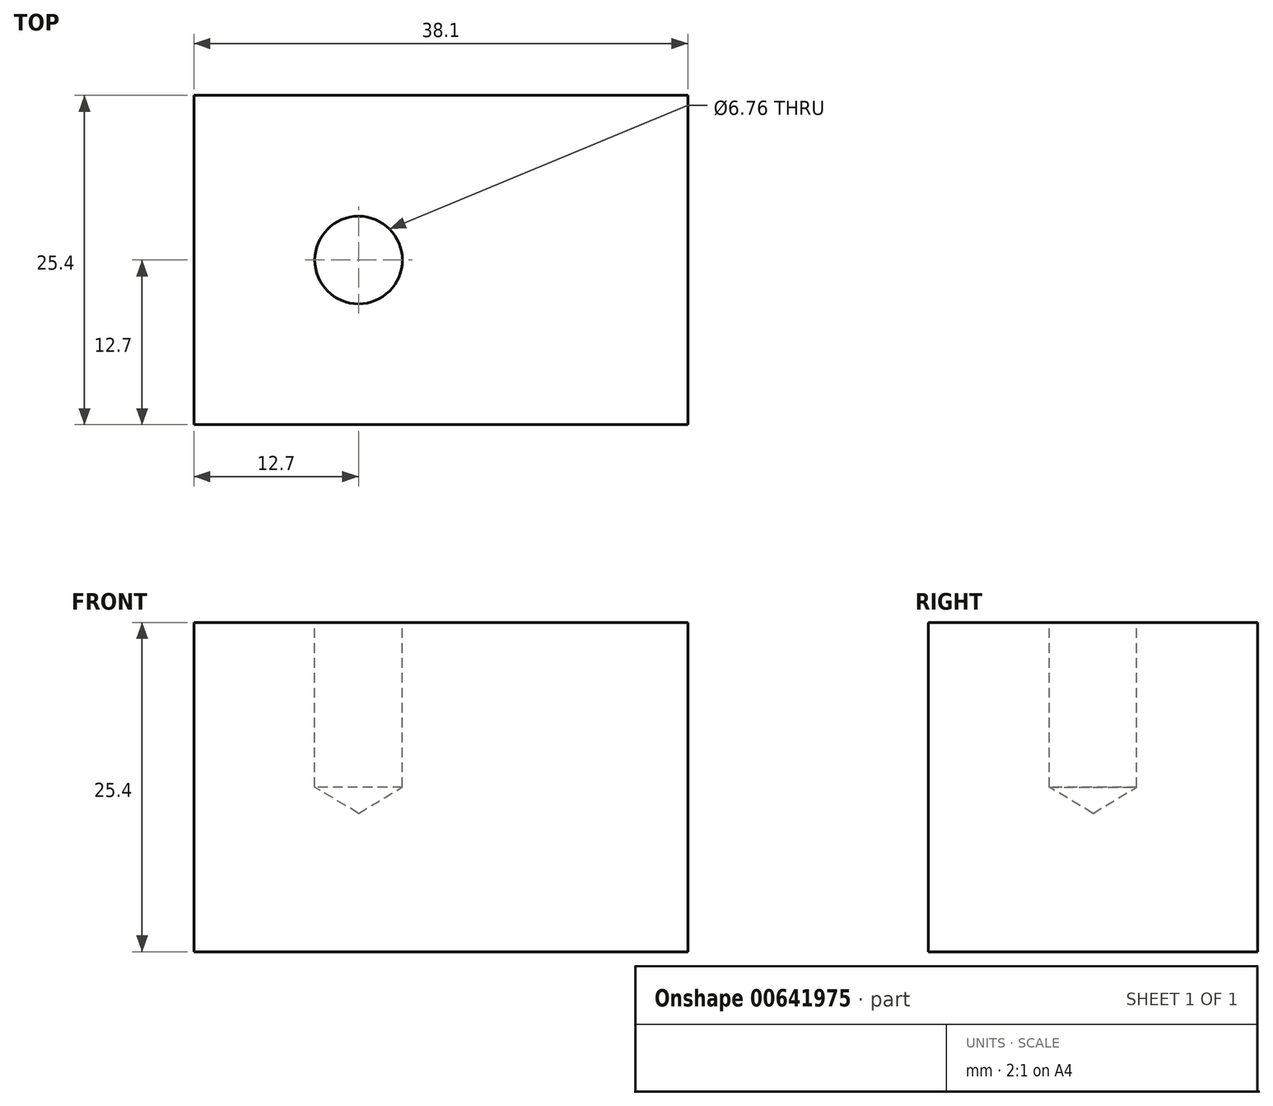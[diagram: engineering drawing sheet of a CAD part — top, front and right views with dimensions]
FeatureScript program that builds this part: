
annotation { "Feature Type Name" : "Feature", "Feature Type Description" : "" }
export const myFeature = defineFeature(function(context is Context, id is Id, definition is map)
    precondition{}
    {
        {
            var Q0;
            Q0=qCreatedBy(makeId("Top.planeOp"),FACE);
            var sketch = newSketch(context, id + "F0", { "sketchPlane" : qUnion([Q0])});
            skLineSegment(sketch, "E0.bottom", {"start": v(-50.8, 38.1) * mm, "end": v(-12.7, 38.1) * mm});
            skLineSegment(sketch, "E0.top", {"start": v(-50.8, 12.7) * mm, "end": v(-12.7, 12.7) * mm});
            skLineSegment(sketch, "E0.left", {"start": v(-50.8, 38.1) * mm, "end": v(-50.8, 12.7) * mm});
            skLineSegment(sketch, "E0.right", {"start": v(-12.7, 38.1) * mm, "end": v(-12.7, 12.7) * mm});
            skLineSegment(sketch, "E1.bottom", {"start": v(-12.7, 12.7) * mm, "end": v(0, 12.7) * mm});
            skLineSegment(sketch, "E1.top", {"start": v(-12.7, 0) * mm, "end": v(0, 0) * mm});
            skLineSegment(sketch, "E1.left", {"start": v(-12.7, 12.7) * mm, "end": v(-12.7, 0) * mm});
            skLineSegment(sketch, "E1.right", {"start": v(0, 12.7) * mm, "end": v(0, 0) * mm});
            skSolve(sketch);
        }
        {
            var Q0;
            Q0=makeQuery(id+"F0.imprint","IMPRINT",FACE,{"disambiguationData":[TD([[makeQuery(id+"F0.imprint","IMPRINT",EDGE,{"derivedFrom":sQuery(id+"F0.wireOp",EDGE,"E0.bottom")}),-1.0]])]});
            extrude(context, id + "F1", {"entities" : qUnion([Q0]), "depth" : 25.4 * mm, "offsetDistance" : 25.4 * mm});
        }
        {
            var Q0;
            Q0=makeQuery(id+"F1.opExtrude","CAP_FACE",FACE,{"disambiguationData":[OSD([sQuery(id+"F0.wireOp",EDGE,"E0.bottom"),sQuery(id+"F0.wireOp",EDGE,"E0.top"),sQuery(id+"F0.wireOp",EDGE,"E0.left"),sQuery(id+"F0.wireOp",EDGE,"E0.right")])],"isStart":false});
            var sketch = newSketch(context, id + "F2", { "sketchPlane" : qUnion([Q0])});
            skPoint(sketch, "E2", {"position": v(-38.1, 25.4) * mm});
            skSolve(sketch);
        }
        {
            var Q0;
            Q0=sQuery(id+"F2.wireOp",VERTEX,"E2");
            var Q1;
            Q1=makeQuery(id+"F1.opExtrude","SWEPT_BODY",BODY,{"disambiguationData":[OSD([sQuery(id+"F0.wireOp",EDGE,"E0.bottom"),sQuery(id+"F0.wireOp",EDGE,"E0.top"),sQuery(id+"F0.wireOp",EDGE,"E0.left"),sQuery(id+"F0.wireOp",EDGE,"E0.right")])]});
            hole(context, id + "F3", {"style" : HoleStyle.SIMPLE, "endStyle" : HoleEndStyle.BLIND, "standardTappedOrClearance" : lookupTablePath({ "standard" : "ANSI", "fit" : "Normal (ASME)", "size" : "1/4", "type" : "Clearance" }), "standardBlindInLast" : lookupTablePath({ "fit" : "Free", "standard" : "ANSI", "size" : "1/4", "type" : "Clearance" }), "holeDiameter" : 6.76 * mm, "majorDiameter" : 6.35 * mm, "holeDepth" : 12.7 * mm, "isTappedThrough" : true, "tappedDepth" : 12.7 * mm, "tapClearance" : 3, "locations" : qUnion([Q0]), "scope" : qUnion([Q1])});
        }
    });
